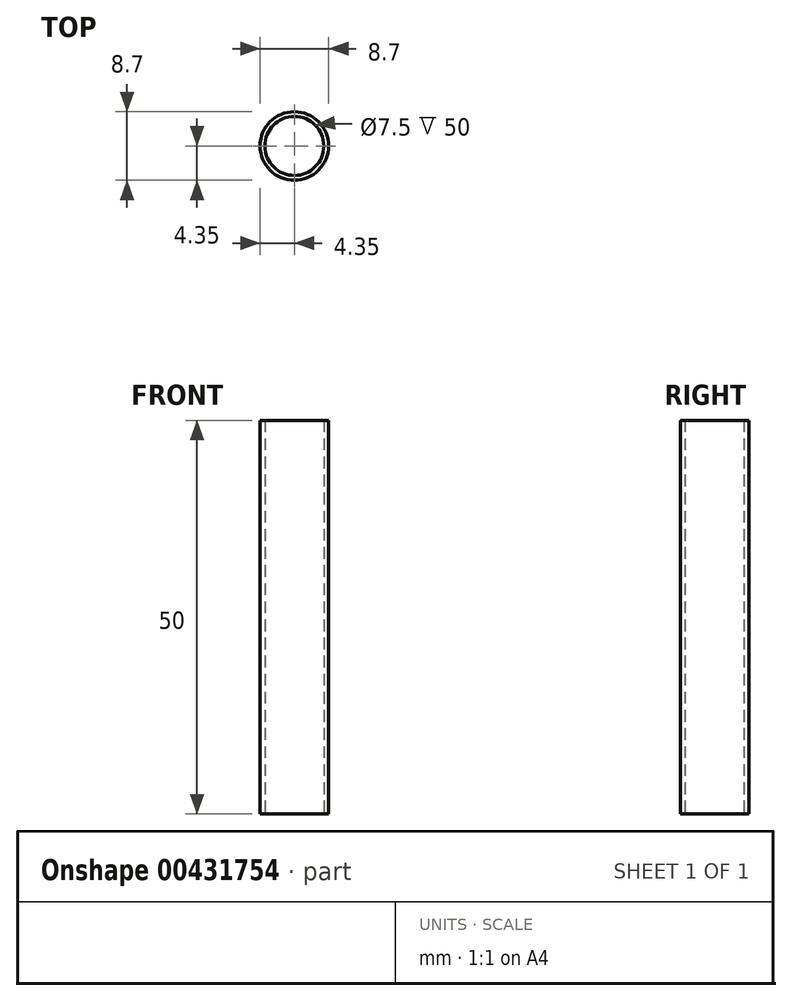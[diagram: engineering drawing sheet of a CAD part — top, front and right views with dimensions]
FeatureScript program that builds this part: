
annotation { "Feature Type Name" : "Feature", "Feature Type Description" : "" }
export const myFeature = defineFeature(function(context is Context, id is Id, definition is map)
    precondition{}
    {
        {
            var Q0;
            Q0=qCreatedBy(makeId("Top.planeOp"),FACE);
            var sketch = newSketch(context, id + "F0", { "sketchPlane" : qUnion([Q0])});
            skCircle(sketch, "E0", {"center": v(0, 0) * mm, "radius": 3.75 * mm});
            skCircle(sketch, "E1", {"center": v(0, 0) * mm, "radius": 4.35 * mm});
            skSolve(sketch);
        }
        {
            var Q0;
            Q0 = qSketchRegion(id + "F0", true);
            extrude(context, id + "F1", {"entities" : qUnion([Q0]), "depth" : 50 * mm});
        }
    });
